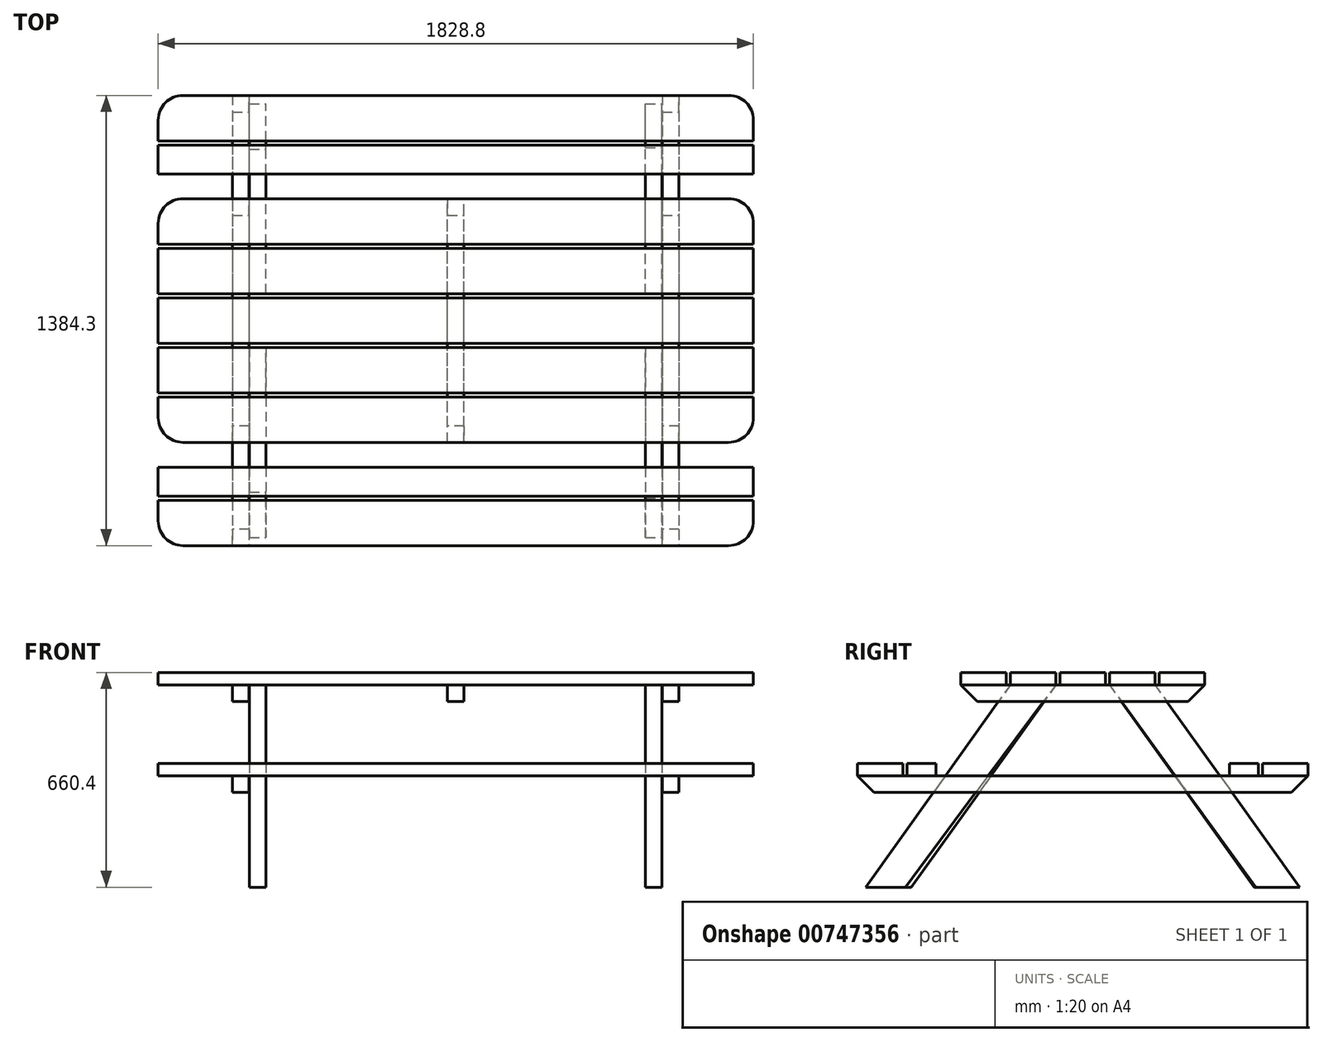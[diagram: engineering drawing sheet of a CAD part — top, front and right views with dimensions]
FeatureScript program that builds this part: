
annotation { "Feature Type Name" : "Feature", "Feature Type Description" : "" }
export const myFeature = defineFeature(function(context is Context, id is Id, definition is map)
    precondition{}
    {
        {
            var Q0;
            Q0=qCreatedBy(makeId("Top.planeOp"),FACE);
            cPlane(context, id + "F0", {"entities" : qUnion([Q0]), "cplaneType" : CPlaneType.OFFSET, "offset" : 622.3 * mm, "width" : 152.4 * mm, "height" : 152.4 * mm});
        }
        {
            var Q0;
            Q0=qCreatedBy(makeId("Top.planeOp"),FACE);
            cPlane(context, id + "F1", {"entities" : qUnion([Q0]), "cplaneType" : CPlaneType.OFFSET, "offset" : 342.9 * mm, "width" : 152.4 * mm, "height" : 152.4 * mm});
        }
        {
            var Q0;
            Q0=qCreatedBy(id+"F0.planeOp",FACE);
            var sketch = newSketch(context, id + "F2", { "sketchPlane" : qUnion([Q0])});
            skLineSegment(sketch, "E0.bottom", {"start": v(914.4, 69.85) * mm, "end": v(-914.4, 69.85) * mm});
            skLineSegment(sketch, "E0.top", {"start": v(914.4, -69.85) * mm, "end": v(-914.4, -69.85) * mm});
            skLineSegment(sketch, "E0.left", {"start": v(914.4, 69.85) * mm, "end": v(914.4, -69.85) * mm});
            skLineSegment(sketch, "E0.right", {"start": v(-914.4, 69.85) * mm, "end": v(-914.4, -69.85) * mm});
            skPoint(sketch, "E0.middle", {"position": v(0, 0) * mm});
            skSolve(sketch);
        }
        {
            var Q0;
            Q0=qCreatedBy(id+"F0.planeOp",FACE);
            var sketch = newSketch(context, id + "F3", { "sketchPlane" : qUnion([Q0])});
            skLineSegment(sketch, "E1.bottom", {"start": v(914.4, 82.55) * mm, "end": v(-914.4, 82.55) * mm});
            skLineSegment(sketch, "E1.top", {"start": v(914.4, 222.25) * mm, "end": v(-914.4, 222.25) * mm});
            skLineSegment(sketch, "E1.left", {"start": v(914.4, 82.55) * mm, "end": v(914.4, 222.25) * mm});
            skLineSegment(sketch, "E1.right", {"start": v(-914.4, 82.55) * mm, "end": v(-914.4, 222.25) * mm});
            skPoint(sketch, "E1.middle", {"position": v(0, 152.4) * mm});
            skLineSegment(sketch, "E2.bottom", {"start": v(914.4, 234.95) * mm, "end": v(-914.4, 234.95) * mm});
            skLineSegment(sketch, "E2.top", {"start": v(914.4, 374.65) * mm, "end": v(-914.4, 374.65) * mm});
            skLineSegment(sketch, "E2.left", {"start": v(914.4, 234.95) * mm, "end": v(914.4, 374.65) * mm});
            skLineSegment(sketch, "E2.right", {"start": v(-914.4, 234.95) * mm, "end": v(-914.4, 374.65) * mm});
            skPoint(sketch, "E2.middle", {"position": v(0, 304.8) * mm});
            skLineSegment(sketch, "E3.bottom", {"start": v(914.4, -222.25) * mm, "end": v(-914.4, -222.25) * mm});
            skLineSegment(sketch, "E3.top", {"start": v(914.4, -82.55) * mm, "end": v(-914.4, -82.55) * mm});
            skLineSegment(sketch, "E3.left", {"start": v(914.4, -222.25) * mm, "end": v(914.4, -82.55) * mm});
            skLineSegment(sketch, "E3.right", {"start": v(-914.4, -222.25) * mm, "end": v(-914.4, -82.55) * mm});
            skPoint(sketch, "E3.middle", {"position": v(0, -152.4) * mm});
            skLineSegment(sketch, "E4.bottom", {"start": v(914.4, -374.65) * mm, "end": v(-914.4, -374.65) * mm});
            skLineSegment(sketch, "E4.top", {"start": v(914.4, -234.95) * mm, "end": v(-914.4, -234.95) * mm});
            skLineSegment(sketch, "E4.left", {"start": v(914.4, -374.65) * mm, "end": v(914.4, -234.95) * mm});
            skLineSegment(sketch, "E4.right", {"start": v(-914.4, -374.65) * mm, "end": v(-914.4, -234.95) * mm});
            skPoint(sketch, "E4.middle", {"position": v(0, -304.8) * mm});
            skSolve(sketch);
        }
        {
            var Q0;
            Q0=makeQuery(id+"F3.imprint","IMPRINT",FACE,{"disambiguationData":[TD([[makeQuery(id+"F3.imprint","IMPRINT",EDGE,{"derivedFrom":sQuery(id+"F3.wireOp",EDGE,"E2.bottom")}),-1.0]])]});
            var Q1;
            Q1=makeQuery(id+"F3.imprint","IMPRINT",FACE,{"disambiguationData":[TD([[makeQuery(id+"F3.imprint","IMPRINT",EDGE,{"derivedFrom":sQuery(id+"F3.wireOp",EDGE,"E1.bottom")}),-1.0]])]});
            var Q2;
            Q2=makeQuery(id+"F2.imprint","IMPRINT",FACE,{"disambiguationData":[TD([[makeQuery(id+"F2.imprint","IMPRINT",EDGE,{"derivedFrom":sQuery(id+"F2.wireOp",EDGE,"E0.bottom")}),1.0]])]});
            var Q3;
            Q3=makeQuery(id+"F3.imprint","IMPRINT",FACE,{"disambiguationData":[TD([[makeQuery(id+"F3.imprint","IMPRINT",EDGE,{"derivedFrom":sQuery(id+"F3.wireOp",EDGE,"E3.bottom")}),-1.0]])]});
            var Q4;
            Q4=makeQuery(id+"F3.imprint","IMPRINT",FACE,{"disambiguationData":[TD([[makeQuery(id+"F3.imprint","IMPRINT",EDGE,{"derivedFrom":sQuery(id+"F3.wireOp",EDGE,"E4.bottom")}),-1.0]])]});
            extrude(context, id + "F4", {"entities" : qUnion([Q0, Q1, Q2, Q3, Q4]), "depth" : 38.1 * mm, "offsetDistance" : 25.4 * mm});
        }
        {
            var Q0;
            Q0=makeQuery(id+"F4.opExtrude","SWEPT_EDGE",EDGE,{"disambiguationData":[OSD([sQuery(id+"F3.wireOp",EDGE,"E4.bottom"),sQuery(id+"F3.wireOp",EDGE,"E4.left")])]});
            var Q1;
            Q1=makeQuery(id+"F4.opExtrude","SWEPT_EDGE",EDGE,{"disambiguationData":[OSD([sQuery(id+"F3.wireOp",EDGE,"E2.top"),sQuery(id+"F3.wireOp",EDGE,"E2.left")])]});
            var Q2;
            Q2=makeQuery(id+"F4.opExtrude","SWEPT_EDGE",EDGE,{"disambiguationData":[OSD([sQuery(id+"F3.wireOp",EDGE,"E4.bottom"),sQuery(id+"F3.wireOp",EDGE,"E4.right")])]});
            var Q3;
            Q3=makeQuery(id+"F4.opExtrude","SWEPT_EDGE",EDGE,{"disambiguationData":[OSD([sQuery(id+"F3.wireOp",EDGE,"E2.top"),sQuery(id+"F3.wireOp",EDGE,"E2.right")])]});
            fillet(context, id + "F5", {"entities" : qUnion([Q0, Q1, Q2, Q3]), "radius" : 76.2 * mm, "tangentPropagation" : true, "allowEdgeOverflow" : false});
        }
        {
            var Q0;
            Q0=qCreatedBy(id+"F1.planeOp",FACE);
            var sketch = newSketch(context, id + "F6", { "sketchPlane" : qUnion([Q0])});
            skLineSegment(sketch, "E5.bottom", {"start": v(914.4, 450.85) * mm, "end": v(-914.4, 450.85) * mm});
            skLineSegment(sketch, "E5.top", {"start": v(914.4, 539.75) * mm, "end": v(-914.4, 539.75) * mm});
            skLineSegment(sketch, "E5.left", {"start": v(914.4, 450.85) * mm, "end": v(914.4, 539.75) * mm});
            skLineSegment(sketch, "E5.right", {"start": v(-914.4, 450.85) * mm, "end": v(-914.4, 539.75) * mm});
            skPoint(sketch, "E5.middle", {"position": v(0, 495.3) * mm});
            skLineSegment(sketch, "E6.bottom", {"start": v(914.4, -539.75) * mm, "end": v(-914.4, -539.75) * mm});
            skLineSegment(sketch, "E6.top", {"start": v(914.4, -450.85) * mm, "end": v(-914.4, -450.85) * mm});
            skLineSegment(sketch, "E6.left", {"start": v(914.4, -539.75) * mm, "end": v(914.4, -450.85) * mm});
            skLineSegment(sketch, "E6.right", {"start": v(-914.4, -539.75) * mm, "end": v(-914.4, -450.85) * mm});
            skPoint(sketch, "E6.middle", {"position": v(0, -495.3) * mm});
            skLineSegment(sketch, "E7.bottom", {"start": v(914.4, 552.45) * mm, "end": v(-914.4, 552.45) * mm});
            skLineSegment(sketch, "E7.top", {"start": v(914.4, 692.15) * mm, "end": v(-914.4, 692.15) * mm});
            skLineSegment(sketch, "E7.left", {"start": v(914.4, 552.45) * mm, "end": v(914.4, 692.15) * mm});
            skLineSegment(sketch, "E7.right", {"start": v(-914.4, 552.45) * mm, "end": v(-914.4, 692.15) * mm});
            skPoint(sketch, "E7.middle", {"position": v(0, 622.3) * mm});
            skLineSegment(sketch, "E8.bottom", {"start": v(-914.4, -692.15) * mm, "end": v(914.4, -692.15) * mm});
            skLineSegment(sketch, "E8.top", {"start": v(-914.4, -552.45) * mm, "end": v(914.4, -552.45) * mm});
            skLineSegment(sketch, "E8.left", {"start": v(-914.4, -692.15) * mm, "end": v(-914.4, -552.45) * mm});
            skLineSegment(sketch, "E8.right", {"start": v(914.4, -692.15) * mm, "end": v(914.4, -552.45) * mm});
            skPoint(sketch, "E8.middle", {"position": v(0, -622.3) * mm});
            skSolve(sketch);
        }
        {
            var Q0;
            Q0 = qSketchRegion(id + "F6", true);
            extrude(context, id + "F7", {"entities" : qUnion([Q0]), "depth" : 38.1 * mm, "offsetDistance" : 25.4 * mm});
        }
        {
            var Q0;
            Q0=makeQuery(id+"F7.opExtrude","SWEPT_EDGE",EDGE,{"disambiguationData":[OSD([sQuery(id+"F6.wireOp",EDGE,"E8.bottom"),sQuery(id+"F6.wireOp",EDGE,"E8.left")])]});
            var Q1;
            Q1=makeQuery(id+"F7.opExtrude","SWEPT_EDGE",EDGE,{"disambiguationData":[OSD([sQuery(id+"F6.wireOp",EDGE,"E7.top"),sQuery(id+"F6.wireOp",EDGE,"E7.right")])]});
            var Q2;
            Q2=makeQuery(id+"F7.opExtrude","SWEPT_EDGE",EDGE,{"disambiguationData":[OSD([sQuery(id+"F6.wireOp",EDGE,"E7.top"),sQuery(id+"F6.wireOp",EDGE,"E7.left")])]});
            var Q3;
            Q3=makeQuery(id+"F7.opExtrude","SWEPT_EDGE",EDGE,{"disambiguationData":[OSD([sQuery(id+"F6.wireOp",EDGE,"E8.bottom"),sQuery(id+"F6.wireOp",EDGE,"E8.right")])]});
            fillet(context, id + "F8", {"entities" : qUnion([Q0, Q1, Q2, Q3]), "radius" : 76.2 * mm, "tangentPropagation" : true, "allowEdgeOverflow" : false});
        }
        {
            var Q0;
            Q0=qCreatedBy(id+"F0.planeOp",FACE);
            var sketch = newSketch(context, id + "F9", { "sketchPlane" : qUnion([Q0])});
            skLineSegment(sketch, "E9.bottom", {"start": v(-635, 374.65) * mm, "end": v(-685.8, 374.65) * mm});
            skLineSegment(sketch, "E9.top", {"start": v(-635, -374.65) * mm, "end": v(-685.8, -374.65) * mm});
            skLineSegment(sketch, "E9.left", {"start": v(-635, 374.65) * mm, "end": v(-635, -374.65) * mm});
            skLineSegment(sketch, "E9.right", {"start": v(-685.8, 374.65) * mm, "end": v(-685.8, -374.65) * mm});
            skPoint(sketch, "E9.middle", {"position": v(-660.4, 0) * mm});
            skLineSegment(sketch, "E10.bottom", {"start": v(635, 374.65) * mm, "end": v(685.8, 374.65) * mm});
            skLineSegment(sketch, "E10.top", {"start": v(635, -374.65) * mm, "end": v(685.8, -374.65) * mm});
            skLineSegment(sketch, "E10.left", {"start": v(635, 374.65) * mm, "end": v(635, -374.65) * mm});
            skLineSegment(sketch, "E10.right", {"start": v(685.8, 374.65) * mm, "end": v(685.8, -374.65) * mm});
            skPoint(sketch, "E10.middle", {"position": v(660.4, 0) * mm});
            skLineSegment(sketch, "E11.bottom", {"start": v(25.4, -374.65) * mm, "end": v(-25.4, -374.65) * mm});
            skLineSegment(sketch, "E11.top", {"start": v(25.4, 374.65) * mm, "end": v(-25.4, 374.65) * mm});
            skLineSegment(sketch, "E11.left", {"start": v(25.4, -374.65) * mm, "end": v(25.4, 374.65) * mm});
            skLineSegment(sketch, "E11.right", {"start": v(-25.4, -374.65) * mm, "end": v(-25.4, 374.65) * mm});
            skPoint(sketch, "E11.middle", {"position": v(0, 0) * mm});
            skSolve(sketch);
        }
        {
            var Q0;
            Q0 = qSketchRegion(id + "F9", true);
            extrude(context, id + "F10", {"entities" : qUnion([Q0]), "oppositeDirection" : true, "depth" : 50.8 * mm, "offsetDistance" : 25.4 * mm});
        }
        {
            var Q0;
            Q0=qCreatedBy(id+"F1.planeOp",FACE);
            var sketch = newSketch(context, id + "F11", { "sketchPlane" : qUnion([Q0])});
            skLineSegment(sketch, "E12.bottom", {"start": v(-635, 692.15) * mm, "end": v(-685.8, 692.15) * mm});
            skLineSegment(sketch, "E12.top", {"start": v(-635, -692.15) * mm, "end": v(-685.8, -692.15) * mm});
            skLineSegment(sketch, "E12.left", {"start": v(-635, 692.15) * mm, "end": v(-635, -692.15) * mm});
            skLineSegment(sketch, "E12.right", {"start": v(-685.8, 692.15) * mm, "end": v(-685.8, -692.15) * mm});
            skPoint(sketch, "E12.middle", {"position": v(-660.4, 0) * mm});
            skLineSegment(sketch, "E13.bottom", {"start": v(685.8, 692.15) * mm, "end": v(635, 692.15) * mm});
            skLineSegment(sketch, "E13.top", {"start": v(685.8, -692.15) * mm, "end": v(635, -692.15) * mm});
            skLineSegment(sketch, "E13.left", {"start": v(685.8, 692.15) * mm, "end": v(685.8, -692.15) * mm});
            skLineSegment(sketch, "E13.right", {"start": v(635, 692.15) * mm, "end": v(635, -692.15) * mm});
            skPoint(sketch, "E13.middle", {"position": v(660.4, 0) * mm});
            skSolve(sketch);
        }
        {
            var Q0;
            Q0=makeQuery(id+"F10.opExtrude","CAP_EDGE",EDGE,{"disambiguationData":[OSD([sQuery(id+"F9.wireOp",EDGE,"E9.top")])],"isStart":false});
            var Q1;
            Q1=makeQuery(id+"F10.opExtrude","CAP_EDGE",EDGE,{"disambiguationData":[OSD([sQuery(id+"F9.wireOp",EDGE,"E11.bottom")])],"isStart":false});
            var Q2;
            Q2=makeQuery(id+"F10.opExtrude","CAP_EDGE",EDGE,{"disambiguationData":[OSD([sQuery(id+"F9.wireOp",EDGE,"E10.top")])],"isStart":false});
            var Q3;
            Q3=makeQuery(id+"F10.opExtrude","CAP_EDGE",EDGE,{"disambiguationData":[OSD([sQuery(id+"F9.wireOp",EDGE,"E10.bottom")])],"isStart":false});
            var Q4;
            Q4=makeQuery(id+"F10.opExtrude","CAP_EDGE",EDGE,{"disambiguationData":[OSD([sQuery(id+"F9.wireOp",EDGE,"E11.top")])],"isStart":false});
            var Q5;
            Q5=makeQuery(id+"F10.opExtrude","CAP_EDGE",EDGE,{"disambiguationData":[OSD([sQuery(id+"F9.wireOp",EDGE,"E9.bottom")])],"isStart":false});
            chamfer(context, id + "F12", {"entities" : qUnion([Q0, Q1, Q2, Q3, Q4, Q5]), "width" : 50.8 * mm, "tangentPropagation" : true});
        }
        {
            var Q0;
            Q0 = qSketchRegion(id + "F11", true);
            extrude(context, id + "F13", {"entities" : qUnion([Q0]), "oppositeDirection" : true, "depth" : 50.8 * mm, "offsetDistance" : 25.4 * mm});
        }
        {
            var Q0;
            Q0=makeQuery(id+"F13.opExtrude","CAP_EDGE",EDGE,{"disambiguationData":[OSD([sQuery(id+"F11.wireOp",EDGE,"E12.top")])],"isStart":false});
            var Q1;
            Q1=makeQuery(id+"F13.opExtrude","CAP_EDGE",EDGE,{"disambiguationData":[OSD([sQuery(id+"F11.wireOp",EDGE,"E13.top")])],"isStart":false});
            var Q2;
            Q2=makeQuery(id+"F13.opExtrude","CAP_EDGE",EDGE,{"disambiguationData":[OSD([sQuery(id+"F11.wireOp",EDGE,"E13.bottom")])],"isStart":false});
            var Q3;
            Q3=makeQuery(id+"F13.opExtrude","CAP_EDGE",EDGE,{"disambiguationData":[OSD([sQuery(id+"F11.wireOp",EDGE,"E12.bottom")])],"isStart":false});
            chamfer(context, id + "F14", {"entities" : qUnion([Q0, Q1, Q2, Q3]), "width" : 50.8 * mm, "tangentPropagation" : true});
        }
        {
            var Q0;
            Q0=qCreatedBy(id+"F0.planeOp",FACE);
            var sketch = newSketch(context, id + "F15", { "sketchPlane" : qUnion([Q0])});
            skLineSegment(sketch, "E14.bottom", {"start": v(-633.73, -222.34) * mm, "end": v(-583.16, -222.34) * mm});
            skLineSegment(sketch, "E14.top", {"start": v(-633.73, -82.64) * mm, "end": v(-583.16, -82.64) * mm});
            skLineSegment(sketch, "E14.left", {"start": v(-633.73, -222.34) * mm, "end": v(-633.73, -82.64) * mm});
            skLineSegment(sketch, "E14.right", {"start": v(-583.16, -222.34) * mm, "end": v(-583.16, -82.64) * mm});
            skLineSegment(sketch, "E15.bottom", {"start": v(-633.73, 81.49) * mm, "end": v(-583.16, 81.49) * mm});
            skLineSegment(sketch, "E15.top", {"start": v(-633.73, 221.19) * mm, "end": v(-583.16, 221.19) * mm});
            skLineSegment(sketch, "E15.left", {"start": v(-633.73, 81.49) * mm, "end": v(-633.73, 221.19) * mm});
            skLineSegment(sketch, "E15.right", {"start": v(-583.16, 81.49) * mm, "end": v(-583.16, 221.19) * mm});
            skLineSegment(sketch, "E16.bottom", {"start": v(582.93, -223.29) * mm, "end": v(633.73, -223.29) * mm});
            skLineSegment(sketch, "E16.top", {"start": v(582.93, -83.59) * mm, "end": v(633.73, -83.59) * mm});
            skLineSegment(sketch, "E16.left", {"start": v(582.93, -223.29) * mm, "end": v(582.93, -83.59) * mm});
            skLineSegment(sketch, "E16.right", {"start": v(633.73, -223.29) * mm, "end": v(633.73, -83.59) * mm});
            skLineSegment(sketch, "E17.bottom", {"start": v(582.93, 81.55) * mm, "end": v(633.73, 81.55) * mm});
            skLineSegment(sketch, "E17.top", {"start": v(582.93, 221.25) * mm, "end": v(633.73, 221.25) * mm});
            skLineSegment(sketch, "E17.left", {"start": v(582.93, 81.55) * mm, "end": v(582.93, 221.25) * mm});
            skLineSegment(sketch, "E17.right", {"start": v(633.73, 81.55) * mm, "end": v(633.73, 221.25) * mm});
            skSolve(sketch);
        }
        {
            var Q0;
            Q0=qCreatedBy(makeId("Top.planeOp"),FACE);
            var sketch = newSketch(context, id + "F16", { "sketchPlane" : qUnion([Q0])});
            skLineSegment(sketch, "E18.bottom", {"start": v(-633.73, -666.75) * mm, "end": v(-582.93, -666.75) * mm});
            skLineSegment(sketch, "E18.top", {"start": v(-633.73, -527.05) * mm, "end": v(-582.93, -527.05) * mm});
            skLineSegment(sketch, "E18.left", {"start": v(-633.73, -666.75) * mm, "end": v(-633.73, -527.05) * mm});
            skLineSegment(sketch, "E18.right", {"start": v(-582.93, -666.75) * mm, "end": v(-582.93, -527.05) * mm});
            skLineSegment(sketch, "E19.bottom", {"start": v(-633.73, 527.05) * mm, "end": v(-582.93, 527.05) * mm});
            skLineSegment(sketch, "E19.top", {"start": v(-633.73, 666.75) * mm, "end": v(-582.93, 666.75) * mm});
            skLineSegment(sketch, "E19.left", {"start": v(-633.73, 527.05) * mm, "end": v(-633.73, 666.75) * mm});
            skLineSegment(sketch, "E19.right", {"start": v(-582.93, 527.05) * mm, "end": v(-582.93, 666.75) * mm});
            skLineSegment(sketch, "E20.bottom", {"start": v(582.93, 531.08) * mm, "end": v(633.73, 531.08) * mm});
            skLineSegment(sketch, "E20.top", {"start": v(582.93, 666.75) * mm, "end": v(633.73, 666.75) * mm});
            skLineSegment(sketch, "E20.left", {"start": v(582.93, 531.08) * mm, "end": v(582.93, 666.75) * mm});
            skLineSegment(sketch, "E20.right", {"start": v(633.73, 531.08) * mm, "end": v(633.73, 666.75) * mm});
            skLineSegment(sketch, "E21.bottom", {"start": v(582.93, -666.75) * mm, "end": v(633.73, -666.75) * mm});
            skLineSegment(sketch, "E21.top", {"start": v(582.93, -545.86) * mm, "end": v(633.73, -545.86) * mm});
            skLineSegment(sketch, "E21.left", {"start": v(582.93, -666.75) * mm, "end": v(582.93, -545.86) * mm});
            skLineSegment(sketch, "E21.right", {"start": v(633.73, -666.75) * mm, "end": v(633.73, -545.86) * mm});
            skSolve(sketch);
        }
        {
            var Q1;
            Q1=makeQuery(id+"F15.imprint","IMPRINT",FACE,{"disambiguationData":[TD([[makeQuery(id+"F15.imprint","IMPRINT",EDGE,{"derivedFrom":sQuery(id+"F15.wireOp",EDGE,"E17.bottom")}),1.0]])]});
            var Q2;
            Q2=makeQuery(id+"F16.imprint","IMPRINT",FACE,{"disambiguationData":[TD([[makeQuery(id+"F16.imprint","IMPRINT",EDGE,{"derivedFrom":sQuery(id+"F16.wireOp",EDGE,"E20.bottom")}),1.0]])]});
            loft(context, id + "F17", {"operationType" : NewBodyOperationType.ADD, "sheetProfilesArray" : [{ "sheetProfileEntities" : qUnion([Q1]) }, { "sheetProfileEntities" : qUnion([Q2]) }]});
        }
        {
            var Q1;
            Q1=makeQuery(id+"F15.imprint","IMPRINT",FACE,{"disambiguationData":[TD([[makeQuery(id+"F15.imprint","IMPRINT",EDGE,{"derivedFrom":sQuery(id+"F15.wireOp",EDGE,"E15.bottom")}),1.0]])]});
            var Q2;
            Q2=makeQuery(id+"F16.imprint","IMPRINT",FACE,{"disambiguationData":[TD([[makeQuery(id+"F16.imprint","IMPRINT",EDGE,{"derivedFrom":sQuery(id+"F16.wireOp",EDGE,"E19.bottom")}),1.0]])]});
            loft(context, id + "F18", {"operationType" : NewBodyOperationType.ADD, "sheetProfilesArray" : [{ "sheetProfileEntities" : qUnion([Q1]) }, { "sheetProfileEntities" : qUnion([Q2]) }]});
        }
        {
            var Q1;
            Q1=makeQuery(id+"F15.imprint","IMPRINT",FACE,{"disambiguationData":[TD([[makeQuery(id+"F15.imprint","IMPRINT",EDGE,{"derivedFrom":sQuery(id+"F15.wireOp",EDGE,"E16.bottom")}),1.0]])]});
            var Q2;
            Q2=makeQuery(id+"F16.imprint","IMPRINT",FACE,{"disambiguationData":[TD([[makeQuery(id+"F16.imprint","IMPRINT",EDGE,{"derivedFrom":sQuery(id+"F16.wireOp",EDGE,"E21.bottom")}),1.0]])]});
            loft(context, id + "F19", {"operationType" : NewBodyOperationType.ADD, "sheetProfilesArray" : [{ "sheetProfileEntities" : qUnion([Q1]) }, { "sheetProfileEntities" : qUnion([Q2]) }]});
        }
        {
            var Q1;
            Q1=makeQuery(id+"F15.imprint","IMPRINT",FACE,{"disambiguationData":[TD([[makeQuery(id+"F15.imprint","IMPRINT",EDGE,{"derivedFrom":sQuery(id+"F15.wireOp",EDGE,"E14.bottom")}),1.0]])]});
            var Q2;
            Q2=makeQuery(id+"F16.imprint","IMPRINT",FACE,{"disambiguationData":[TD([[makeQuery(id+"F16.imprint","IMPRINT",EDGE,{"derivedFrom":sQuery(id+"F16.wireOp",EDGE,"E18.bottom")}),1.0]])]});
            loft(context, id + "F20", {"operationType" : NewBodyOperationType.ADD, "sheetProfilesArray" : [{ "sheetProfileEntities" : qUnion([Q1]) }, { "sheetProfileEntities" : qUnion([Q2]) }]});
        }
    });
